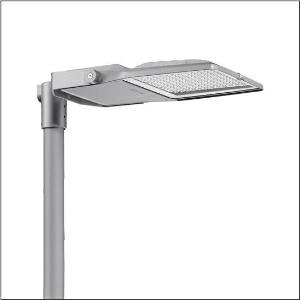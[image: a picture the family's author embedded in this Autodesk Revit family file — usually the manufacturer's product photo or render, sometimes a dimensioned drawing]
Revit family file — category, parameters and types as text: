
# Revit family: floodlight_fl_21_iq_midi___pl64_5xa7781f4e3a_1626
name_source: partatom
category: Lighting Fixtures
units: mm (PartAtom-declared; Revit-internal decimal feet)

## family parameters
Cut with Voids When Loaded = No
Host = Face
Light Source = No
Part Type = Normal
Room Calculation Point = No
Round Connector Dimension = Use Diameter
Shared = No

## types (1)
- --- (1 x LED, 36050 lm, 270.2 W, 4000K)
    Apparent Load = 270 VA
    CIE Flux Codes = 28 80 98 100 100
    Color Rendering = 70
    Color Temperature = 4000K
    Default Elevation = 1800 mm
    Description = Floodlight FL 21 iQ midi, floodlight, primary light control with lens, of PMMA, primary optical cover: protective disc, of toughened safety glass, transparent, light distribution: PL64, light emission: direct distribution, installation type: surface-mounted, LED, High Power LED, rated luminous flux: 36.050lm, luminous efficacy: 133lm/W, light colour: 740, colour temperature: 4000K, control gear: ECG iQ, control: optimised constant luminous flux control (CLO 2.0), Desk-Remote (wireless, voltage-free reading and setting of iQ features in the workshop via application-optimized NFC function/RFID function), Light-Fading, Smart-Wire, Night-Set, Lumen-Switch, Temp-Guard, Auto-Match, with terminal, 6-pole, mains connection: 220..240V, AC, 50/60Hz, start of lifetime: 270W, end of service life: 287W, reduction: 118W, luminaire housing, of diecast aluminium, powder-coated, Siteco® metallic grey (DB 702S), corrosivity category C5 mid according to DIN EN ISO 12944, sealing non-destructively replaceable, please order mast flange separately, mast bracket, of steel, galvanised, powder-coated, Siteco® metallic grey (DB 702S), protection rating (complete): IP66, insulation class (complete): insulation class II (safety insulation), certification: CE, ENEC, VDE, protection symbol: D, impact resistance: IK08, permissible operating ambient temperature: -40..+40°C, permissible operating ambient temperature for outdoor applications: -40..+50°C, standard: DIN EN 12944, LABS conformity tested according to VDMA 24364:2018-05, packaging unit: 1 piece

Light Distribution: PL64
    Height = 76 mm
    Lamp = 1 x LED
    Lamp Light Flux = 36050 lm
    Lamp Power = 270.2 W
    Lamp count = 1
    Length = 657 mm
    Luminous efficacy = 133 lm/W
    Manufacturer = Siteco
    ModVariant = No
    Model = 5XA7781F4E3A
    Number of Poles = 1
    OnlyDefault = Yes
    Power Factor = 1
    Product Name = Floodlight FL 21 iQ midi | PL64
    Product group = floodlight | pylon annexe
    ProductGroupID = 6200
    Protection Class = Protection class II
    Protection Degree = IP 66
    RLX_Detail_Level = 1
    RLX_Emergency_Light_Flux = 0 lm
    RLX_Emergency_Type = 0
    RLX_Emergency_Type_DB = No
    RlxData = <blob elided: 153901 chars, md5=83be3bf3>
    Socket = socket
    Standby Power = 0 W
    System Light Flux = 36050 lm
    System Power = 270 W
    Type Comments = factory setting: luminous flux: 100 % | dim-lin: 254 | 620 mA
    Type Image = l_1007123.jpg
    URL = http://relux.com
    VarID = @adj_075639
    Voltage = 0 V
    Weight = 0.00 kg
    Width = 442 mm

## geometry (parser evidence)
native form markers: Blend x4, Sweep x12
no freeform markers — native parametric forms only
